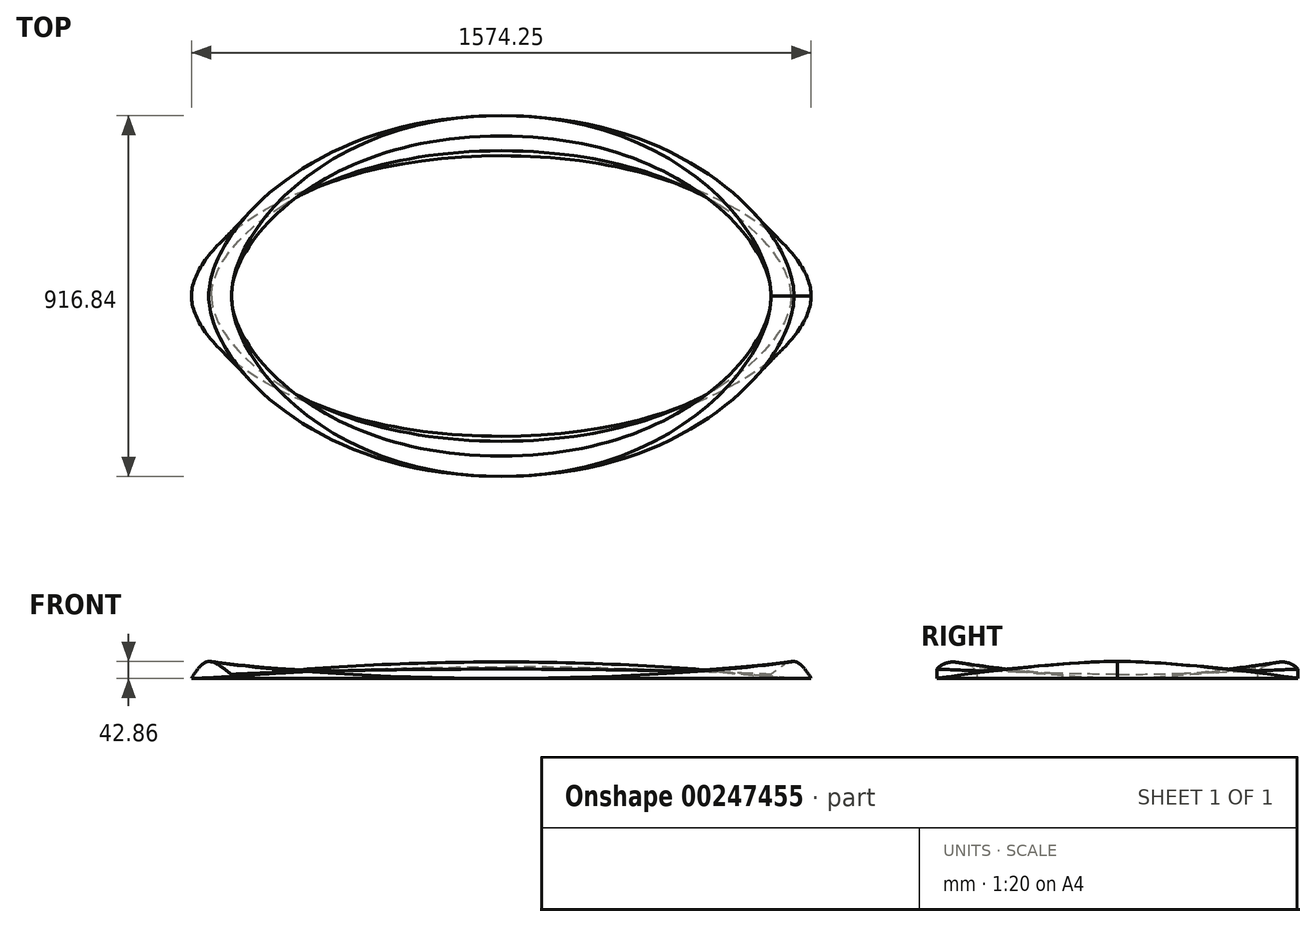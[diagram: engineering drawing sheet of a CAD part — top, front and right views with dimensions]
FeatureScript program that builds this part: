
annotation { "Feature Type Name" : "Feature", "Feature Type Description" : "" }
export const myFeature = defineFeature(function(context is Context, id is Id, definition is map)
    precondition{}
    {
        {
            var Q0;
            Q0=qCreatedBy(makeId("Top.planeOp"),FACE);
            var sketch = newSketch(context, id + "F0", { "sketchPlane" : qUnion([Q0])});
            skEllipticalArc(sketch, "E0", {});
            skLineSegment(sketch, "E1", {"start": v(-0.13, 0) * mm, "end": v(0, 0) * mm});
            skPoint(sketch, "E2.end.orphan", {"position": v(0, -355.6) * mm});
            skLineSegment(sketch, "E3", {"start": v(-0.13, 355.6) * mm, "end": v(0, 355.6) * mm});
            skEllipticalArc(sketch, "E4", {});
            const initialGuessF0  = {"E0": [0, 0, 1, 0, 0.6858, 0.3556, 1.57098151198114, 3.141592653589793], "E4": [0, 0, 1, 0, 0.6858, 0.3556, 3.141592653589793, 1.5707963267948966]};
            skSetInitialGuess(sketch, initialGuessF0);
            skSolve(sketch);
        }
        {
            var Q0;
            Q0=sQuery(id+"F0.wireOp",EDGE,"E0");
            var Q1;
            Q1=sQuery(id+"F0.wireOp",VERTEX,"E0.start");
            cPlane(context, id + "F1", {"entities" : qUnion([Q0, Q1]), "cplaneType" : CPlaneType.CURVE_POINT, "offset" : 25.4 * mm, "width" : 152.4 * mm, "height" : 152.4 * mm});
        }
        {
            var Q0;
            Q0=qCreatedBy(id+"F1.planeOp",FACE);
            var sketch = newSketch(context, id + "F2", { "sketchPlane" : qUnion([Q0])});
            skLineSegment(sketch, "E5", {"start": v(-356.72, 0) * mm, "end": v(-458.42, 0) * mm});
            skLineSegment(sketch, "E6", {"start": v(-458.42, 0) * mm, "end": v(-458.42, 23.47) * mm});
            skArc(sketch, "E7", {"start": v(-407, 40.23) * mm, "mid": v(-434.97, 38.77) * mm, "end": v(-458.42, 23.47) * mm});
            skArc(sketch, "E8", {"start": v(-356.72, 0) * mm, "mid": v(-358.55, 16.36) * mm, "end": v(-369.01, 29.06) * mm});
            skLineSegment(sketch, "E9", {"start": v(-369.01, 29.06) * mm, "end": v(-407, 40.23) * mm});
            skSolve(sketch);
        }
        {
            var Q0;
            Q0=qCreatedBy(makeId("Front.planeOp"),FACE);
            var sketch = newSketch(context, id + "F3", { "sketchPlane" : qUnion([Q0])});
            skLineSegment(sketch, "E10", {"start": v(-787.22, 0) * mm, "end": v(-685.8, 0) * mm});
            skLineSegment(sketch, "E11", {"start": v(-685.8, 0) * mm, "end": v(-685.8, 9.97) * mm});
            skFitSpline(sketch, "E12", {"points": [v(-787.22, 0) * mm, v(-745.05, 42.63) * mm, v(-685.8, 9.97) * mm], "startDerivative": vector(80.2, 125.69) * mm, "endDerivative": vector(132.79, -102.15) * mm});
            skSolve(sketch);
        }
        {
            var Q0;
            Q0=makeQuery(id+"F3.imprint","IMPRINT",FACE,{"disambiguationData":[TD([[makeQuery(id+"F3.imprint","IMPRINT",EDGE,{"derivedFrom":sQuery(id+"F3.wireOp",EDGE,"E10")}),1.0]])]});
            var Q1;
            Q1=makeQuery(id+"F2.imprint","IMPRINT",FACE,{"disambiguationData":[TD([[makeQuery(id+"F2.imprint","IMPRINT",EDGE,{"derivedFrom":sQuery(id+"F2.wireOp",EDGE,"E5")}),-1.0]])]});
            loft(context, id + "F4", {"startCondition" : LoftEndDerivativeType.NORMAL_TO_PROFILE, "startMagnitude" : 1, "endCondition" : LoftEndDerivativeType.NORMAL_TO_PROFILE, "endMagnitude" : 1.9, "sheetProfilesArray" : [{ "sheetProfileEntities" : qUnion([Q0]) }, { "sheetProfileEntities" : qUnion([Q1]) }]});
        }
        {
            var Q0;
            Q0=makeQuery(id+"F4.opLoft","SWEPT_BODY",BODY,{"disambiguationData":[OSD([makeQuery(id+"F2.imprint","IMPRINT",FACE,{"disambiguationData":[TD([[makeQuery(id+"F2.imprint","IMPRINT",EDGE,{"derivedFrom":sQuery(id+"F2.wireOp",EDGE,"E5")}),-1.0]])]}),makeQuery(id+"F3.imprint","IMPRINT",FACE,{"disambiguationData":[TD([[makeQuery(id+"F3.imprint","IMPRINT",EDGE,{"derivedFrom":sQuery(id+"F3.wireOp",EDGE,"E10")}),1.0]])]})])]});
            var Q1;
            Q1=makeQuery(id+"F4.opLoft","CAP_FACE",FACE,{"disambiguationData":[OSD([makeQuery(id+"F2.imprint","IMPRINT",FACE,{"disambiguationData":[TD([[makeQuery(id+"F2.imprint","IMPRINT",EDGE,{"derivedFrom":sQuery(id+"F2.wireOp",EDGE,"E5")}),-1.0]])]})])],"isStart":true});
            mirror(context, id + "F5", {"operationType" : NewBodyOperationType.ADD, "entities" : qUnion([Q0]), "mirrorPlane" : qUnion([Q1])});
        }
        {
            var Q0;
            Q0=makeQuery(id+"F4.opLoft","SWEPT_BODY",BODY,{"disambiguationData":[OSD([makeQuery(id+"F2.imprint","IMPRINT",FACE,{"disambiguationData":[TD([[makeQuery(id+"F2.imprint","IMPRINT",EDGE,{"derivedFrom":sQuery(id+"F2.wireOp",EDGE,"E5")}),-1.0]])]}),makeQuery(id+"F3.imprint","IMPRINT",FACE,{"disambiguationData":[TD([[makeQuery(id+"F3.imprint","IMPRINT",EDGE,{"derivedFrom":sQuery(id+"F3.wireOp",EDGE,"E10")}),1.0]])]})])]});
            var Q1;
            Q1=makeQuery(id+"F4.opLoft","CAP_FACE",FACE,{"disambiguationData":[OSD([makeQuery(id+"F3.imprint","IMPRINT",FACE,{"disambiguationData":[TD([[makeQuery(id+"F3.imprint","IMPRINT",EDGE,{"derivedFrom":sQuery(id+"F3.wireOp",EDGE,"E10")}),1.0]])]})])],"isStart":true});
            mirror(context, id + "F6", {"operationType" : NewBodyOperationType.ADD, "entities" : qUnion([Q0]), "mirrorPlane" : qUnion([Q1])});
        }
    });
